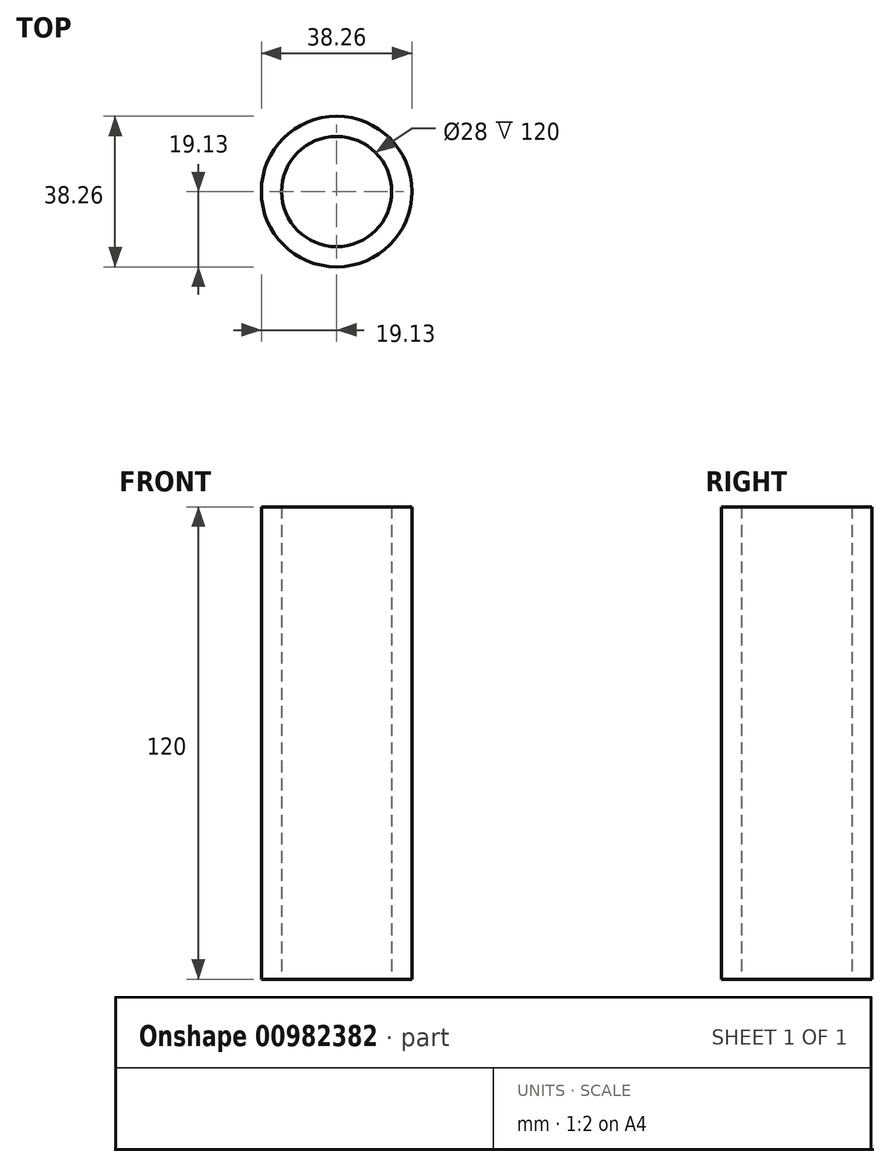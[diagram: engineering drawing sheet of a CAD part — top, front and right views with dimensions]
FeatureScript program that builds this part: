
annotation { "Feature Type Name" : "Feature", "Feature Type Description" : "" }
export const myFeature = defineFeature(function(context is Context, id is Id, definition is map)
    precondition{}
    {
        {
            var Q0;
            Q0=qCreatedBy(makeId("Top.planeOp"),FACE);
            var sketch = newSketch(context, id + "F0", { "sketchPlane" : qUnion([Q0])});
            skCircle(sketch, "E0", {"center": v(0, 0) * mm, "radius": 19.12 * mm});
            skCircle(sketch, "E1", {"center": v(0, 0) * mm, "radius": 14 * mm});
            skSolve(sketch);
        }
        {
            var Q0;
            Q0=makeQuery(id+"F0.imprint","IMPRINT",FACE,{"disambiguationData":[TD([[makeQuery(id+"F0.imprint","IMPRINT",EDGE,{"derivedFrom":sQuery(id+"F0.wireOp",EDGE,"E0")}),1.0]])]});
            extrude(context, id + "F1", {"entities" : qUnion([Q0]), "depth" : 120 * mm, "offsetDistance" : 25 * mm});
        }
    });
